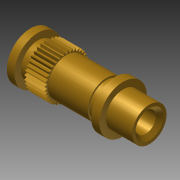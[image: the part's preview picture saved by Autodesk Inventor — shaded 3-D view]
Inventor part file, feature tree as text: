
AUTODESK INVENTOR PART (.ipt)
format: ipt  version: 2013 (Build 170138000, 138)  size: 266,752 bytes
history: native  units: in
note: dims shown in document units (in); Inventor stores cm internally (conversion verified against a paired STEP export)
features: sketch x3, revolve x1, hole x1, chamfer x1, extrude x1
ambient origin geometry x8: Origin, YZ Plane, XZ Plane, XY Plane, X Axis, Y Axis, Z Axis, Center Point
bodies: Solid1 (feature_tree)
feature tree (7):
  revolve  "Revolution1"  Angle=45.0deg
  hole  "Hole1"  [1 undecoded]
  chamfer  "Chamfer1"  [1 undecoded]
  extrude  "Extrusion1"  [1 undecoded]
  sketch  "Sketch1"  dims[d0=90.0deg]
  sketch  "Sketch2"  dims[d1=0.107in d2=0.75in d3=0.375in d4=0.25in d5=0.5635in d6=0.375in d7=0.8108in d8=0.02in d9=0.125in d10=45.0deg]
  sketch  "Sketch3"  dims[d11=0.106in d12=0.0in]
note: 3 required parameter values undecoded (feature->parameter linkage not recoverable at this tier; creation-order binding heuristic only, values carry confidence <= 0.55)
